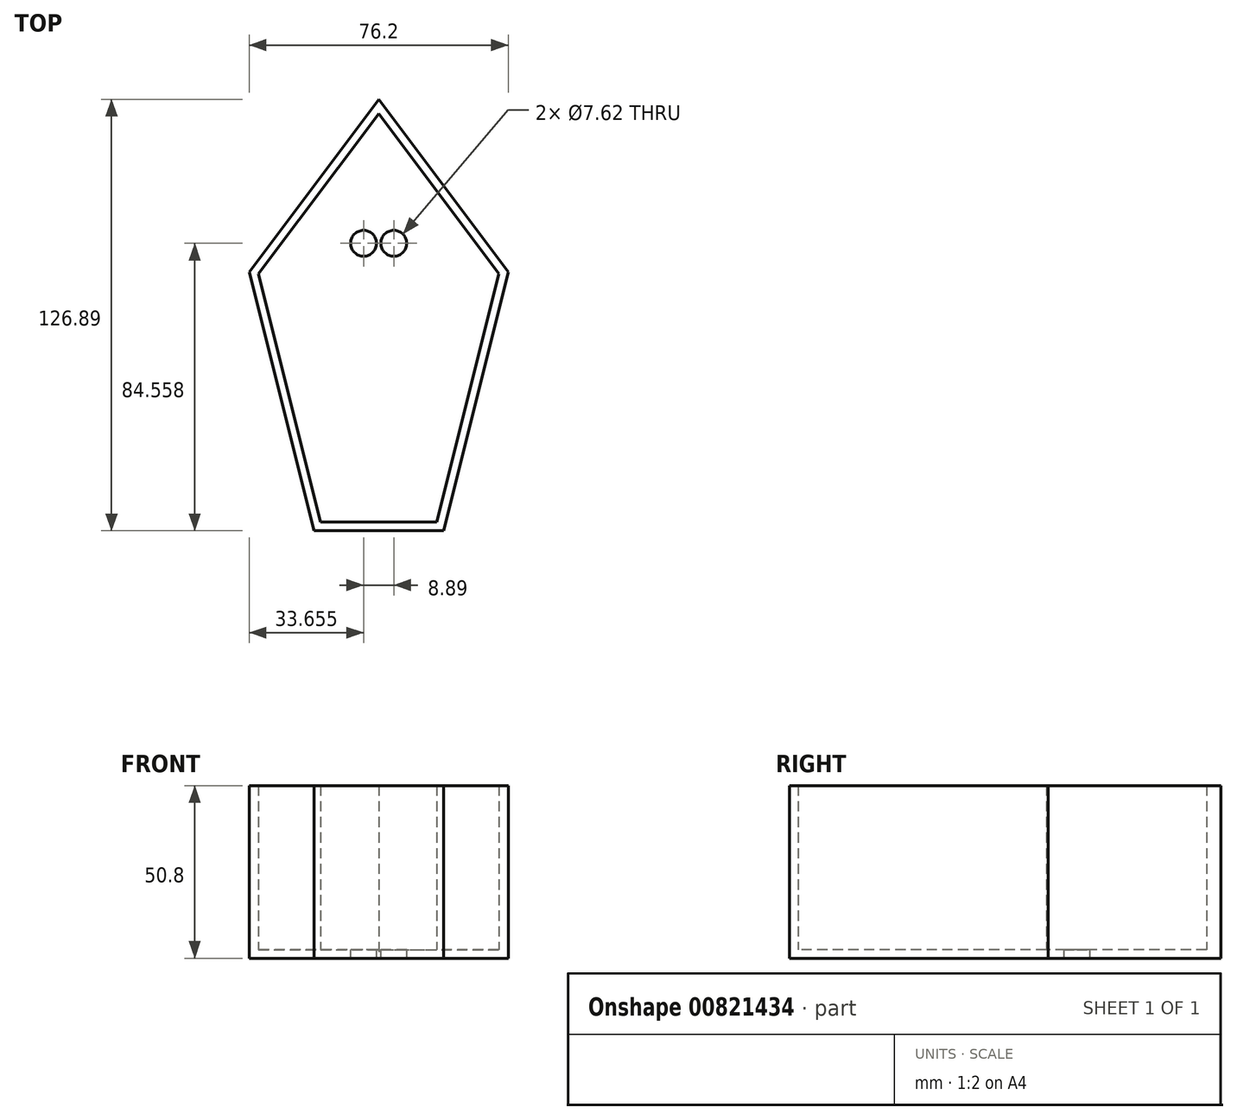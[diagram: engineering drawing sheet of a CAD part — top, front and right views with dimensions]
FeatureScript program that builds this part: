
annotation { "Feature Type Name" : "Feature", "Feature Type Description" : "" }
export const myFeature = defineFeature(function(context is Context, id is Id, definition is map)
    precondition{}
    {
        {
            var Q0;
            Q0=qCreatedBy(makeId("Top.planeOp"),FACE);
            var sketch = newSketch(context, id + "F0", { "sketchPlane" : qUnion([Q0])});
            skLineSegment(sketch, "E0", {"start": v(0, 71.12) * mm, "end": v(0, -55.88) * mm});
            skLineSegment(sketch, "E1", {"start": v(0, 71.12) * mm, "end": v(0, 20.32) * mm});
            skLineSegment(sketch, "E2", {"start": v(0, 20.32) * mm, "end": v(38.1, 20.32) * mm});
            skLineSegment(sketch, "E3", {"start": v(0, 20.32) * mm, "end": v(-38.1, 20.32) * mm});
            skLineSegment(sketch, "E4", {"start": v(0, 71.12) * mm, "end": v(-38.1, 20.32) * mm});
            skLineSegment(sketch, "E5", {"start": v(0, 71.12) * mm, "end": v(38.1, 20.32) * mm});
            skLineSegment(sketch, "E6", {"start": v(-38.1, 20.32) * mm, "end": v(-19.05, -55.77) * mm});
            skPoint(sketch, "E6.endSnap0", {"position": v(-19.05, 20.32) * mm});
            skLineSegment(sketch, "E7", {"start": v(38.1, 20.32) * mm, "end": v(19.05, -55.77) * mm});
            skLineSegment(sketch, "E8", {"start": v(-19.05, -55.77) * mm, "end": v(19.05, -55.77) * mm});
            skSolve(sketch);
        }
        {
            var Q0;
            {var subQ0=sQuery(id+"F0.wireOp",EDGE,"E3");Q0=makeQuery(id+"F0.imprint","IMPRINT",FACE,{"disambiguationData":[TD([[makeQuery(id+"F0.imprint","IMPRINT",EDGE,{"derivedFrom":subQ0}),1.0]])]});}
            var Q1;
            {var subQ0=sQuery(id+"F0.wireOp",EDGE,"E2");Q1=makeQuery(id+"F0.imprint","IMPRINT",FACE,{"disambiguationData":[TD([[makeQuery(id+"F0.imprint","IMPRINT",EDGE,{"derivedFrom":subQ0}),-1.0]])]});}
            var Q2;
            {var subQ0=sQuery(id+"F0.wireOp",EDGE,"E2");Q2=makeQuery(id+"F0.imprint","IMPRINT",FACE,{"disambiguationData":[TD([[makeQuery(id+"F0.imprint","IMPRINT",EDGE,{"derivedFrom":subQ0}),1.0]])]});}
            var Q3;
            {var subQ0=sQuery(id+"F0.wireOp",EDGE,"E3");Q3=makeQuery(id+"F0.imprint","IMPRINT",FACE,{"disambiguationData":[TD([[makeQuery(id+"F0.imprint","IMPRINT",EDGE,{"derivedFrom":subQ0}),-1.0]])]});}
            extrude(context, id + "F1", {"entities" : qUnion([Q0, Q1, Q2, Q3]), "depth" : 50.8 * mm, "offsetDistance" : 25.4 * mm});
        }
        {
            var Q0;
            Q0=makeQuery(id+"F1.opExtrude","CAP_FACE",FACE,{"disambiguationData":[OSD([sQuery(id+"F0.wireOp",EDGE,"E4"),sQuery(id+"F0.wireOp",EDGE,"E5"),sQuery(id+"F0.wireOp",EDGE,"E6"),sQuery(id+"F0.wireOp",EDGE,"E7"),sQuery(id+"F0.wireOp",EDGE,"E8")])],"isStart":false});
            shell(context, id + "F2", {"entities" : qUnion([Q0]), "thickness" : 2.54 * mm});
        }
        {
            var Q0;
            Q0=makeQuery(id+"F2.opShell","OFFSET_FACE",FACE,{"disambiguationData":[OSD([sQuery(id+"F0.wireOp",EDGE,"E4"),sQuery(id+"F0.wireOp",EDGE,"E5"),sQuery(id+"F0.wireOp",EDGE,"E6"),sQuery(id+"F0.wireOp",EDGE,"E7"),sQuery(id+"F0.wireOp",EDGE,"E8")])]});
            var sketch = newSketch(context, id + "F3", { "sketchPlane" : qUnion([Q0])});
            skCircle(sketch, "E9", {"center": v(-4.44, 28.79) * mm, "radius": 3.81 * mm});
            skCircle(sketch, "E10", {"center": v(4.45, 28.79) * mm, "radius": 3.81 * mm});
            skSolve(sketch);
        }
        {
            var Q0;
            Q0=makeQuery(id+"F3.imprint","IMPRINT",FACE,{"disambiguationData":[TD([[makeQuery(id+"F3.imprint","IMPRINT",EDGE,{"derivedFrom":sQuery(id+"F3.wireOp",EDGE,"E10")}),1.0]])]});
            var Q1;
            Q1=makeQuery(id+"F3.imprint","IMPRINT",FACE,{"disambiguationData":[TD([[makeQuery(id+"F3.imprint","IMPRINT",EDGE,{"derivedFrom":sQuery(id+"F3.wireOp",EDGE,"E9")}),1.0]])]});
            extrude(context, id + "F4", {"entities" : qUnion([Q0, Q1]), "operationType" : NewBodyOperationType.REMOVE, "oppositeDirection" : true, "depth" : 25.4 * mm, "offsetDistance" : 25.4 * mm});
        }
    });
